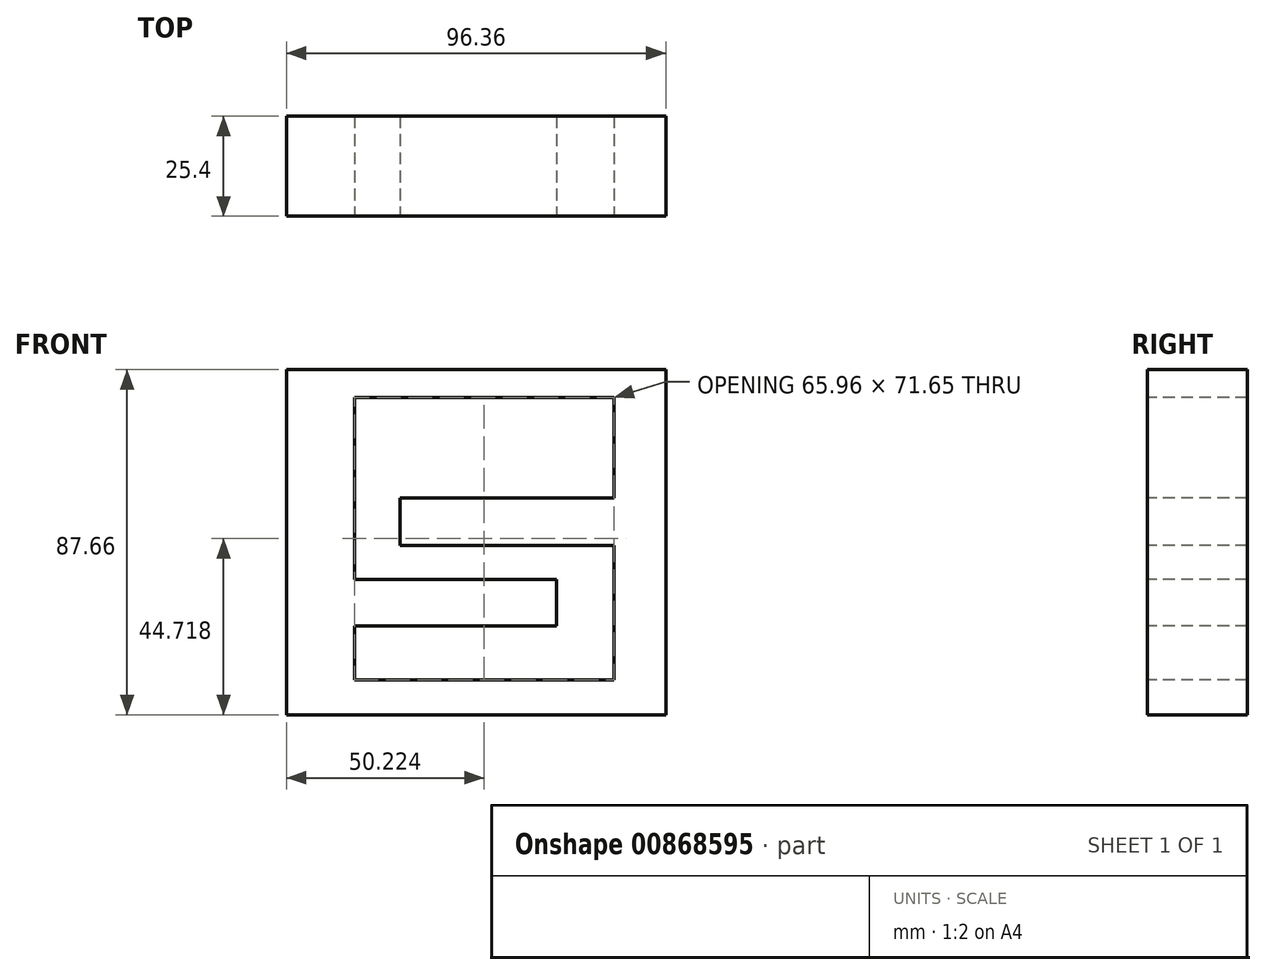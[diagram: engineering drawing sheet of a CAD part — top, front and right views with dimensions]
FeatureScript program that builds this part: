
annotation { "Feature Type Name" : "Feature", "Feature Type Description" : "" }
export const myFeature = defineFeature(function(context is Context, id is Id, definition is map)
    precondition{}
    {
        {
            var Q0;
            Q0=qCreatedBy(makeId("Front.planeOp"),FACE);
            var sketch = newSketch(context, id + "F0", { "sketchPlane" : qUnion([Q0])});
            skLineSegment(sketch, "E0.bottom", {"start": v(-46.5, 44.72) * mm, "end": v(49.87, 44.72) * mm});
            skLineSegment(sketch, "E0.top", {"start": v(-46.5, -42.94) * mm, "end": v(49.87, -42.94) * mm});
            skLineSegment(sketch, "E0.left", {"start": v(-46.5, 44.72) * mm, "end": v(-46.5, -42.94) * mm});
            skLineSegment(sketch, "E0.right", {"start": v(49.87, 44.72) * mm, "end": v(49.87, -42.94) * mm});
            skSolve(sketch);
        }
        {
            var Q0;
            Q0 = qSketchRegion(id + "F0", true);
            extrude(context, id + "F1", {"entities" : qUnion([Q0]), "flatOperationType" : FlatOperationType.REMOVE, "depth" : 25.4 * mm, "offsetDistance" : 25.4 * mm, "domain" : OperationDomain.MODEL});
        }
        {
            var Q0;
            Q0=makeQuery(id+"F1.opExtrude","CAP_FACE",FACE,{"disambiguationData":[OSD([sQuery(id+"F0.wireOp",EDGE,"E0.bottom"),sQuery(id+"F0.wireOp",EDGE,"E0.top"),sQuery(id+"F0.wireOp",EDGE,"E0.left"),sQuery(id+"F0.wireOp",EDGE,"E0.right")])],"isStart":false});
            var sketch = newSketch(context, id + "F2", { "sketchPlane" : qUnion([Q0])});
            skLineSegment(sketch, "E1", {"start": v(-29.25, 37.6) * mm, "end": v(36.72, 37.6) * mm});
            skLineSegment(sketch, "E2", {"start": v(36.72, 37.6) * mm, "end": v(36.72, 12.18) * mm});
            skLineSegment(sketch, "E3", {"start": v(36.72, 12.18) * mm, "end": v(-17.7, 12.18) * mm});
            skLineSegment(sketch, "E4", {"start": v(-17.7, 12.18) * mm, "end": v(-17.7, 0) * mm});
            skLineSegment(sketch, "E5", {"start": v(-17.7, 0) * mm, "end": v(36.72, 0) * mm});
            skLineSegment(sketch, "E6", {"start": v(36.72, 0) * mm, "end": v(36.72, -34.05) * mm});
            skLineSegment(sketch, "E7", {"start": v(36.72, -34.05) * mm, "end": v(-29.25, -34.05) * mm});
            skLineSegment(sketch, "E8", {"start": v(-29.25, -34.05) * mm, "end": v(-29.25, -20.36) * mm});
            skLineSegment(sketch, "E9", {"start": v(-29.25, -20.36) * mm, "end": v(22.14, -20.36) * mm});
            skLineSegment(sketch, "E10", {"start": v(22.14, -20.36) * mm, "end": v(22.14, -8.62) * mm});
            skLineSegment(sketch, "E11", {"start": v(22.14, -8.62) * mm, "end": v(-29.25, -8.62) * mm});
            skLineSegment(sketch, "E12", {"start": v(-29.25, -8.62) * mm, "end": v(-29.25, 37.6) * mm});
            skSolve(sketch);
        }
        {
            var Q0;
            Q0=makeQuery(id+"F2.imprint","IMPRINT",FACE,{"disambiguationData":[TD([[makeQuery(id+"F2.imprint","IMPRINT",EDGE,{"derivedFrom":sQuery(id+"F2.wireOp",EDGE,"E1")}),-1.0]])]});
            var sketch = newSketch(context, id + "F3", { "sketchPlane" : qUnion([Q0])});
            skSolve(sketch);
        }
        {
            var Q0;
            Q0=makeQuery(id+"F3.imprint","IMPRINT",FACE,{"disambiguationData":[TD([[makeQuery(id+"F3.imprint","IMPRINT",EDGE,{"derivedFrom":makeQuery(id+"F2.imprint","IMPRINT",EDGE,{"derivedFrom":sQuery(id+"F2.wireOp",EDGE,"E1")})}),-1.0]])]});
            var Q1;
            Q1=makeQuery(id+"F2.imprint","IMPRINT",FACE,{"disambiguationData":[TD([[makeQuery(id+"F2.imprint","IMPRINT",EDGE,{"derivedFrom":sQuery(id+"F2.wireOp",EDGE,"E1")}),-1.0]])]});
            extrude(context, id + "F4", {"entities" : qUnion([Q0, Q1]), "operationType" : NewBodyOperationType.REMOVE, "oppositeDirection" : true, "depth" : 25.4 * mm, "offsetDistance" : 25.4 * mm});
        }
    });
